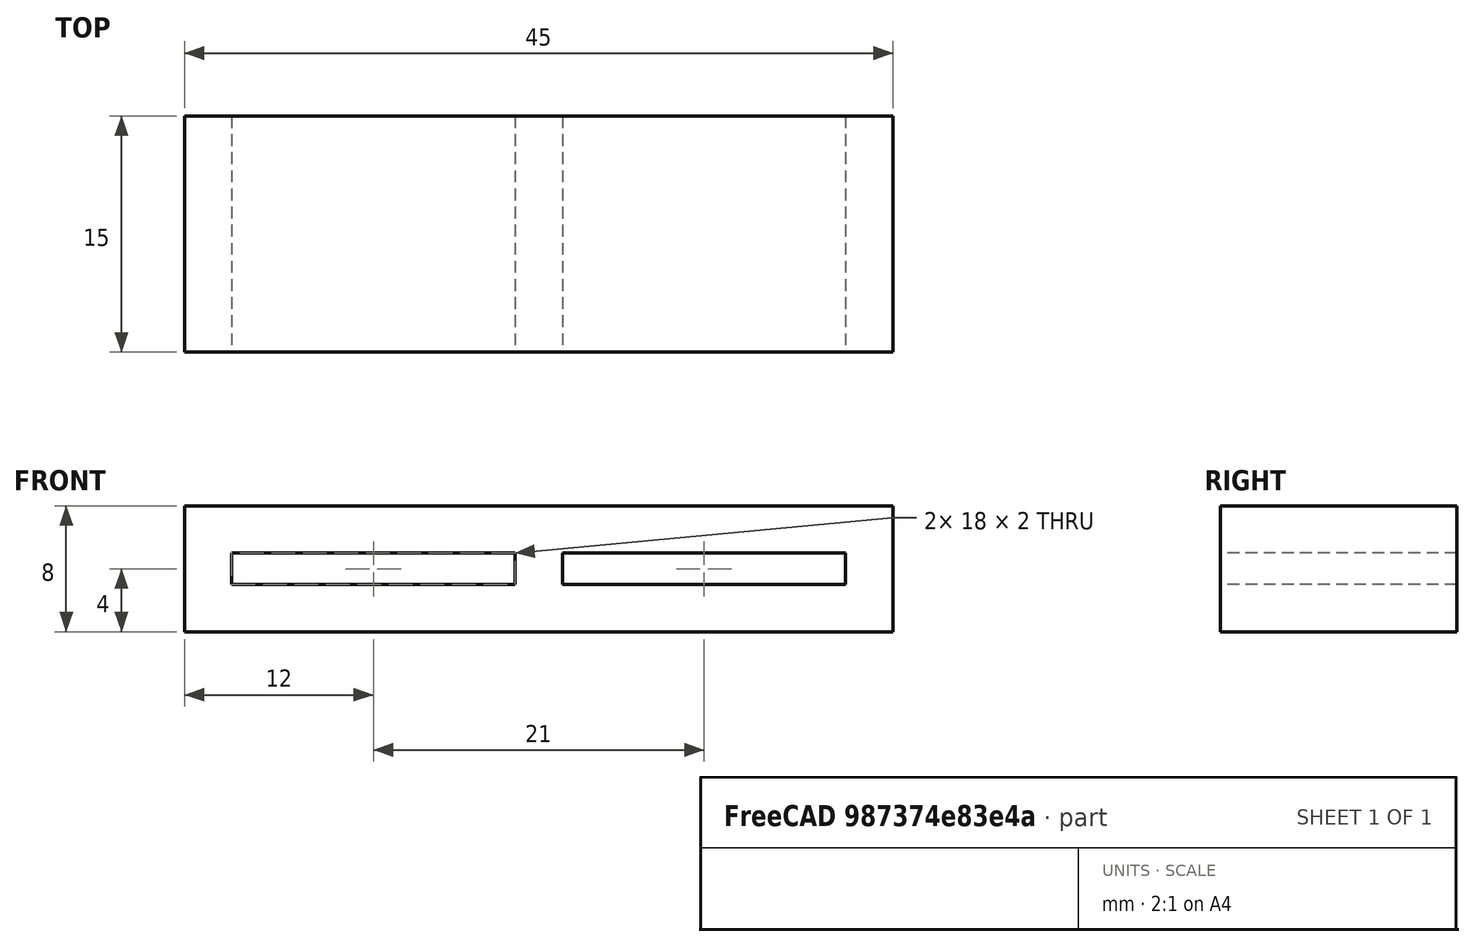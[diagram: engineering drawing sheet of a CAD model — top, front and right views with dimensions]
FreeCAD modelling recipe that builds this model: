
FCSTD DOCUMENT  (FreeCAD 0.21R33771 (Git))
Label: cable-holder-v2
License: All rights reserved
LicenseURL: http://en.wikipedia.org/wiki/All_rights_reserved
objects: Sketcher::SketchObject×1, PartDesign::Pad×1, PartDesign::Body×1, App::Part×1
note: 4 computed .brp shape members not serialized (recipe doc carries the construction recipe); baked Part::Feature solids carry a one-line shape summary decoded from their .brp

FEATURE [Sketcher::SketchObject] Sketch
  FullyConstrained = false
  MapMode = 5
  Placement = pos=(0,0,0) rot=(1,0,0;1.5708rad)
  Support = -> [XZ_Plane001]
  sketch-geometry (12):
    g0: LineSegment StartX=0 StartY=8 StartZ=0 EndX=45 EndY=8 EndZ=0
    g1: LineSegment StartX=45 StartY=8 StartZ=0 EndX=45 EndY=0 EndZ=0
    g2: LineSegment StartX=45 StartY=0 StartZ=0 EndX=0 EndY=0 EndZ=0
    g3: LineSegment StartX=0 StartY=0 StartZ=0 EndX=0 EndY=8 EndZ=0
    g4: LineSegment StartX=3 StartY=5 StartZ=0 EndX=21 EndY=5 EndZ=0
    g5: LineSegment StartX=21 StartY=5 StartZ=0 EndX=21 EndY=3 EndZ=0
    g6: LineSegment StartX=21 StartY=3 StartZ=0 EndX=3 EndY=3 EndZ=0
    g7: LineSegment StartX=3 StartY=3 StartZ=0 EndX=3 EndY=5 EndZ=0
    g8: LineSegment StartX=24 StartY=3 StartZ=0 EndX=42 EndY=3 EndZ=0
    g9: LineSegment StartX=42 StartY=3 StartZ=0 EndX=42 EndY=5 EndZ=0
    g10: LineSegment StartX=42 StartY=5 StartZ=0 EndX=24 EndY=5 EndZ=0
    g11: LineSegment StartX=24 StartY=5 StartZ=0 EndX=24 EndY=3 EndZ=0
  constraints (30):
    c: Coincident(g0,g1)
    c: Coincident(g1,g2)
    c: Coincident(g2,g3)
    c: Coincident(g3,g0)
    c: Horizontal(g0)
    c: Horizontal(g2)
    c: Vertical(g1)
    c: Vertical(g3)
    c: Coincident(g4,g5)
    c: Coincident(g5,g6)
    c: Coincident(g6,g7)
    c: Coincident(g7,g4)
    c: Horizontal(g4)
    c: Horizontal(g6)
    c: Vertical(g5)
    c: Vertical(g7)
    c: DistanceY(g7,g7) = 2
    c: DistanceY(g3,g3) = 8
    c: DistanceX(g0,g0) = 45
    c: DistanceX(g4,g4) = 18
    c: Coincident(g8,g9)
    c: Coincident(g9,g10)
    c: Coincident(g10,g11)
    c: Coincident(g11,g8)
    c: Horizontal(g8)
    c: Horizontal(g10)
    c: Vertical(g9)
    c: Vertical(g11)
    c: DistanceY(g11,g11) = 2
    c: DistanceX(g10,g10) = 18
FEATURE [PartDesign::Pad] Pad
  Direction = (0,-1,2e-16)
  Length = 15
  Length2 = 10
  Placement = pos=(0,0,0) rot=(1,0,0;1.5708rad)
  Profile = -> Sketch
  ReferenceAxis = -> Sketch [N_Axis]
  Type = 0
FEATURE [PartDesign::Body] Body
  Group = -> [Sketch,Pad]
  Origin = -> Origin001
  Tip = -> Pad
FEATURE [App::Part] Part
  Group = -> [Body]
  Origin = -> Origin
